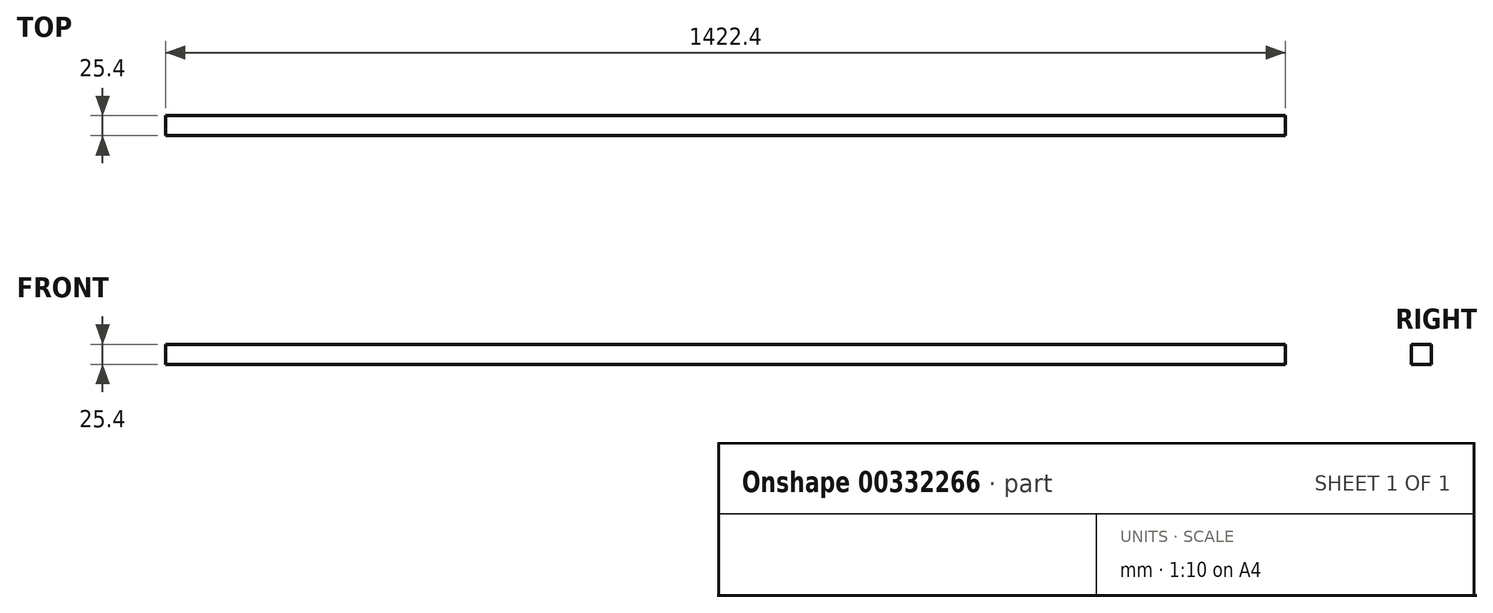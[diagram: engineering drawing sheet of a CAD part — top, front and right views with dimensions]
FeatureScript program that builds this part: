
annotation { "Feature Type Name" : "Feature", "Feature Type Description" : "" }
export const myFeature = defineFeature(function(context is Context, id is Id, definition is map)
    precondition{}
    {
        {
            var Q0;
            Q0=qCreatedBy(makeId("Front.planeOp"),FACE);
            var sketch = newSketch(context, id + "F0", { "sketchPlane" : qUnion([Q0])});
            skLineSegment(sketch, "E0.bottom", {"start": v(711.2, 12.7) * mm, "end": v(-711.2, 12.7) * mm});
            skLineSegment(sketch, "E0.top", {"start": v(711.2, -12.7) * mm, "end": v(-711.2, -12.7) * mm});
            skLineSegment(sketch, "E0.left", {"start": v(711.2, 12.7) * mm, "end": v(711.2, -12.7) * mm});
            skLineSegment(sketch, "E0.right", {"start": v(-711.2, 12.7) * mm, "end": v(-711.2, -12.7) * mm});
            skPoint(sketch, "E0.middle", {"position": v(0, 0) * mm});
            skSolve(sketch);
        }
        {
            var Q0;
            Q0=makeQuery(id+"F0.imprint","IMPRINT",FACE,{"disambiguationData":[TD([[makeQuery(id+"F0.imprint","IMPRINT",EDGE,{"derivedFrom":sQuery(id+"F0.wireOp",EDGE,"E0.bottom")}),1.0]])]});
            extrude(context, id + "F1", {"entities" : qUnion([Q0]), "depth" : 25.4 * mm});
        }
    });
